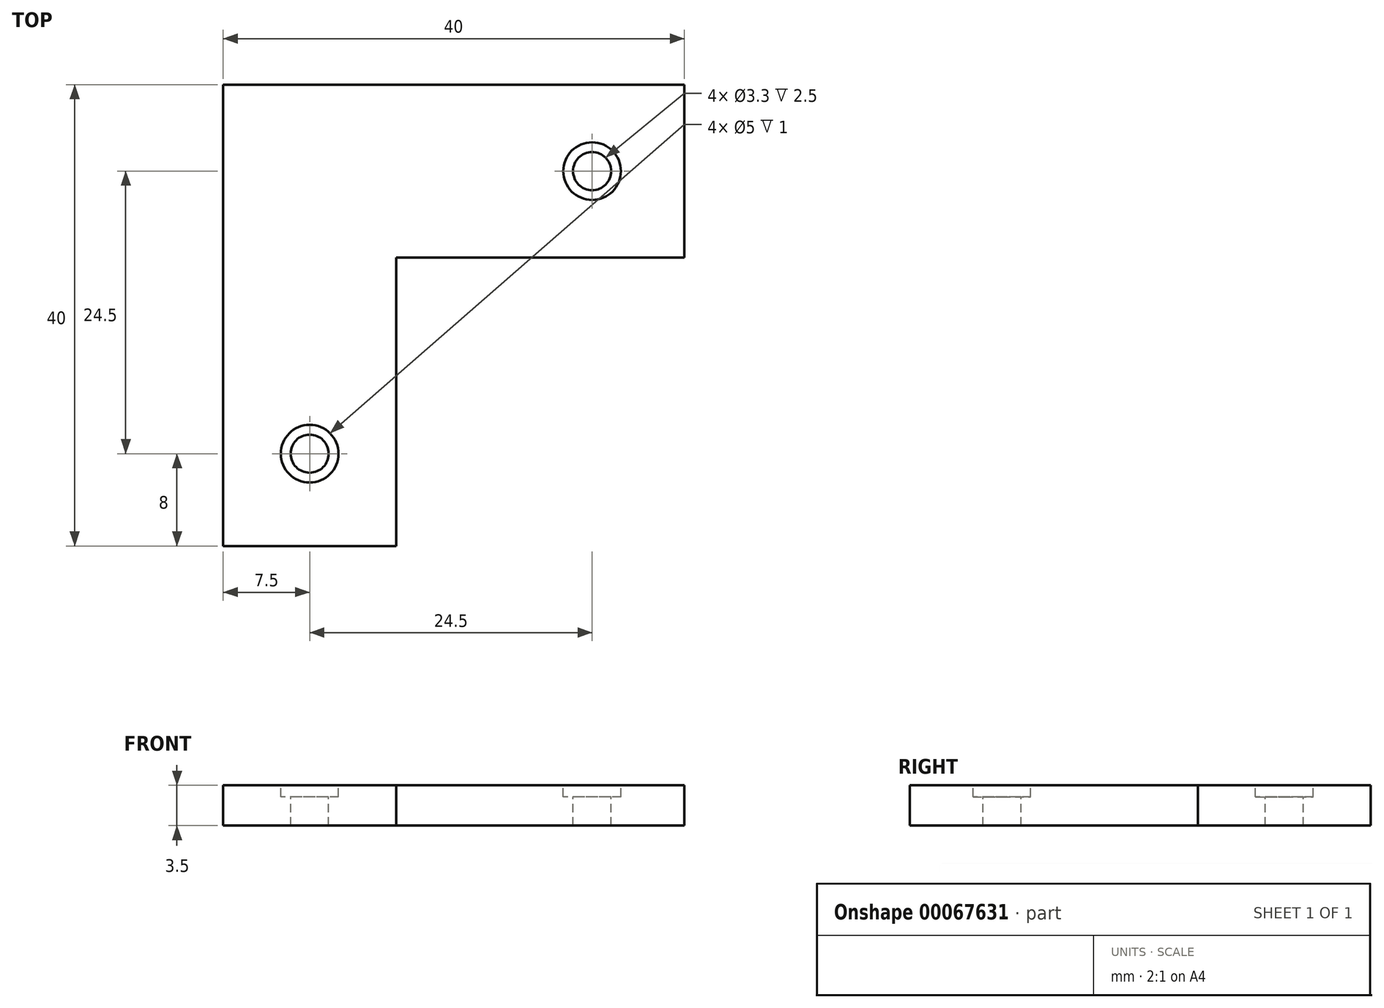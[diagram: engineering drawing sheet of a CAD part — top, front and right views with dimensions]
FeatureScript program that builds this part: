
annotation { "Feature Type Name" : "Feature", "Feature Type Description" : "" }
export const myFeature = defineFeature(function(context is Context, id is Id, definition is map)
    precondition{}
    {
        {
            var Q0;
            Q0=qCreatedBy(makeId("Top.planeOp"),FACE);
            var sketch = newSketch(context, id + "F0", { "sketchPlane" : qUnion([Q0])});
            skLineSegment(sketch, "E0.rect.bottom", {"start": v(-7.5, 20) * mm, "end": v(7.5, 20) * mm});
            skLineSegment(sketch, "E0.rect.top", {"start": v(-7.5, -20) * mm, "end": v(7.5, -20) * mm});
            skLineSegment(sketch, "E0.rect.left", {"start": v(-7.5, 20) * mm, "end": v(-7.5, -20) * mm});
            skLineSegment(sketch, "E0.rect.right", {"start": v(7.5, 20) * mm, "end": v(7.5, -20) * mm});
            skPoint(sketch, "E0.rect.middle", {"position": v(0, 0) * mm});
            skLineSegment(sketch, "E1.bottom", {"start": v(7.5, 20) * mm, "end": v(32.5, 20) * mm});
            skLineSegment(sketch, "E1.top", {"start": v(7.5, 5) * mm, "end": v(32.5, 5) * mm});
            skLineSegment(sketch, "E1.left", {"start": v(7.5, 20) * mm, "end": v(7.5, 5) * mm});
            skLineSegment(sketch, "E1.right", {"start": v(32.5, 20) * mm, "end": v(32.5, 5) * mm});
            skSolve(sketch);
        }
        {
            var Q0;
            Q0=makeQuery(id+"F0.imprint","IMPRINT",FACE,{"disambiguationData":[TD([[makeQuery(id+"F0.imprint","IMPRINT",EDGE,{"derivedFrom":sQuery(id+"F0.wireOp",EDGE,"E0.rect.bottom")}),-1.0]])]});
            var Q1;
            Q1=makeQuery(id+"F0.imprint","IMPRINT",FACE,{"disambiguationData":[TD([[makeQuery(id+"F0.imprint","IMPRINT",EDGE,{"derivedFrom":sQuery(id+"F0.wireOp",EDGE,"E1.bottom")}),-1.0]])]});
            extrude(context, id + "F1", {"entities" : qUnion([Q0, Q1]), "depth" : 3.5 * mm});
        }
        {
            var Q0;
            Q0=makeQuery(id+"F1.opExtrude","CAP_FACE",FACE,{"disambiguationData":[OSD([sQuery(id+"F0.wireOp",EDGE,"E0.rect.bottom"),sQuery(id+"F0.wireOp",EDGE,"E0.rect.top"),sQuery(id+"F0.wireOp",EDGE,"E0.rect.left"),sQuery(id+"F0.wireOp",EDGE,"E0.rect.right"),sQuery(id+"F0.wireOp",EDGE,"E1.bottom"),sQuery(id+"F0.wireOp",EDGE,"E1.top"),sQuery(id+"F0.wireOp",EDGE,"E1.right")])],"isStart":false});
            var sketch = newSketch(context, id + "F2", { "sketchPlane" : qUnion([Q0])});
            skCircle(sketch, "E2", {"center": v(0, -12) * mm, "radius": 1.65 * mm});
            skCircle(sketch, "E3", {"center": v(24.5, 12.5) * mm, "radius": 1.65 * mm});
            skCircle(sketch, "E4", {"center": v(0, 12.5) * mm, "radius": 1.65 * mm});
            skCircle(sketch, "E5", {"center": v(0, -12) * mm, "radius": 2.5 * mm});
            skCircle(sketch, "E6", {"center": v(24.5, 12.5) * mm, "radius": 2.5 * mm});
            skCircle(sketch, "E7", {"center": v(0, 12.5) * mm, "radius": 2.5 * mm});
            skSolve(sketch);
        }
        {
            var Q0;
            Q0=makeQuery(id+"F2.imprint","IMPRINT",FACE,{"disambiguationData":[TD([[makeQuery(id+"F2.imprint","IMPRINT",EDGE,{"derivedFrom":sQuery(id+"F2.wireOp",EDGE,"E2")}),1.0]])]});
            var Q1;
            Q1=makeQuery(id+"F2.imprint","IMPRINT",FACE,{"disambiguationData":[TD([[makeQuery(id+"F2.imprint","IMPRINT",EDGE,{"derivedFrom":sQuery(id+"F2.wireOp",EDGE,"E3")}),1.0]])]});
            extrude(context, id + "F3", {"entities" : qUnion([Q0, Q1]), "operationType" : NewBodyOperationType.REMOVE, "endBound" : BoundingType.UP_TO_NEXT, "oppositeDirection" : true, "depth" : 25 * mm});
        }
        {
            var Q0;
            Q0=makeQuery(id+"F2.imprint","IMPRINT",FACE,{"disambiguationData":[TD([[makeQuery(id+"F2.imprint","IMPRINT",EDGE,{"derivedFrom":sQuery(id+"F2.wireOp",EDGE,"E2")}),-1.0]])]});
            var Q1;
            Q1=makeQuery(id+"F2.imprint","IMPRINT",FACE,{"disambiguationData":[TD([[makeQuery(id+"F2.imprint","IMPRINT",EDGE,{"derivedFrom":sQuery(id+"F2.wireOp",EDGE,"E3")}),-1.0]])]});
            extrude(context, id + "F4", {"entities" : qUnion([Q0, Q1]), "operationType" : NewBodyOperationType.REMOVE, "oppositeDirection" : true, "depth" : 1 * mm});
        }
    });
